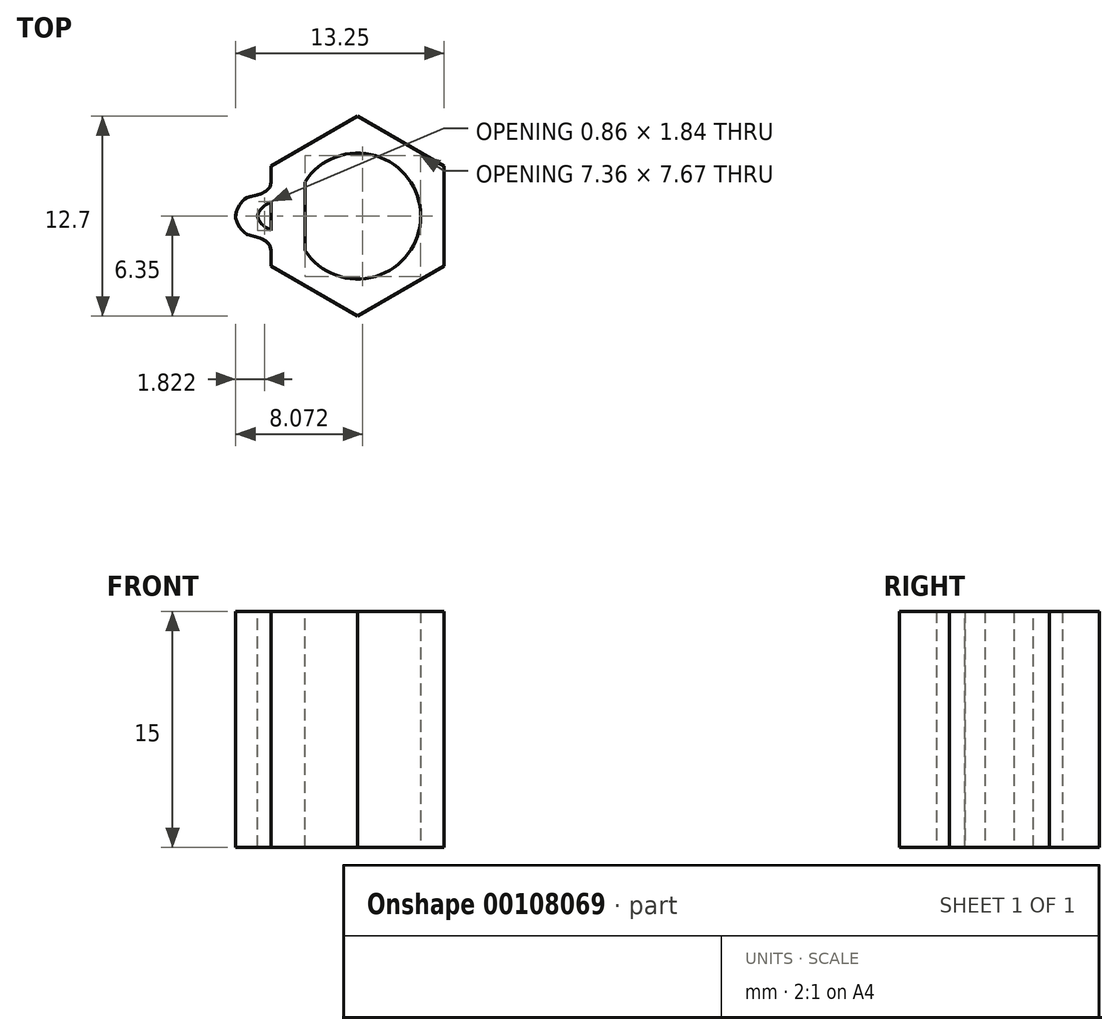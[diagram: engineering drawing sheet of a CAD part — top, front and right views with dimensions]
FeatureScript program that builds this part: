
annotation { "Feature Type Name" : "Feature", "Feature Type Description" : "" }
export const myFeature = defineFeature(function(context is Context, id is Id, definition is map)
    precondition{}
    {
        {
            var Q0;
            Q0=qCreatedBy(makeId("Top.planeOp"),FACE);
            var sketch = newSketch(context, id + "F0", { "sketchPlane" : qUnion([Q0])});
            skCircle(sketch, "E0", {"center": v(0, 0) * mm, "radius": 4 * mm});
            skCircle(sketch, "E1.cCircle", {"center": v(0, 0) * mm, "radius": 5.5 * mm, "construction": true});
            skLineSegment(sketch, "E1.0", {"start": v(5.5, 3.18) * mm, "end": v(5.5, -3.18) * mm});
            skLineSegment(sketch, "E1.1", {"start": v(5.5, -3.18) * mm, "end": v(0, -6.35) * mm});
            skLineSegment(sketch, "E1.2", {"start": v(0, -6.35) * mm, "end": v(-5.5, -3.18) * mm});
            skLineSegment(sketch, "E1.3", {"start": v(-5.5, -3.18) * mm, "end": v(-5.5, 3.18) * mm});
            skLineSegment(sketch, "E1.4", {"start": v(-5.5, 3.18) * mm, "end": v(0, 6.35) * mm});
            skLineSegment(sketch, "E1.5", {"start": v(0, 6.35) * mm, "end": v(5.5, 3.18) * mm});
            skPoint(sketch, "E1.0.midPoint", {"position": v(5.5, 0) * mm});
            skSolve(sketch);
        }
        {
            var Q0;
            Q0=makeQuery(id+"F0.imprint","IMPRINT",FACE,{"disambiguationData":[TD([[makeQuery(id+"F0.imprint","IMPRINT",EDGE,{"derivedFrom":sQuery(id+"F0.wireOp",EDGE,"E0")}),-1.0]])]});
            extrude(context, id + "F1", {"entities" : qUnion([Q0]), "depth" : 15 * mm});
        }
        {
            var Q0;
            Q0=makeQuery(id+"F1.opExtrude","CAP_FACE",FACE,{"disambiguationData":[OSD([sQuery(id+"F0.wireOp",EDGE,"E0"),sQuery(id+"F0.wireOp",EDGE,"E1.0"),sQuery(id+"F0.wireOp",EDGE,"E1.1"),sQuery(id+"F0.wireOp",EDGE,"E1.2"),sQuery(id+"F0.wireOp",EDGE,"E1.3"),sQuery(id+"F0.wireOp",EDGE,"E1.4"),sQuery(id+"F0.wireOp",EDGE,"E1.5")])],"isStart":false});
            var sketch = newSketch(context, id + "F2", { "sketchPlane" : qUnion([Q0])});
            skLineSegment(sketch, "E2", {"start": v(-5.5, 2.18) * mm, "end": v(-3.36, 2.18) * mm});
            skLineSegment(sketch, "E3", {"start": v(-5.5, -2.18) * mm, "end": v(-3.36, -2.18) * mm});
            skLineSegment(sketch, "E4", {"start": v(-5.5, 2.18) * mm, "end": v(-5.5, -2.18) * mm});
            skLineSegment(sketch, "E5", {"start": v(-3.36, 2.18) * mm, "end": v(-3.36, -2.18) * mm});
            skSolve(sketch);
        }
        {
            var Q0;
            {var subQ0=sQuery(id+"F2.wireOp",EDGE,"E2");Q0=makeQuery(id+"F2.imprint","IMPRINT",FACE,{"disambiguationData":[TD([[makeQuery(id+"F2.imprint","IMPRINT",EDGE,{"derivedFrom":subQ0}),-1.0]])]});}
            var Q1;
            Q1=makeQuery(id+"F1.opExtrude","CAP_FACE",FACE,{"disambiguationData":[OSD([sQuery(id+"F0.wireOp",EDGE,"E0"),sQuery(id+"F0.wireOp",EDGE,"E1.0"),sQuery(id+"F0.wireOp",EDGE,"E1.1"),sQuery(id+"F0.wireOp",EDGE,"E1.2"),sQuery(id+"F0.wireOp",EDGE,"E1.3"),sQuery(id+"F0.wireOp",EDGE,"E1.4"),sQuery(id+"F0.wireOp",EDGE,"E1.5")])],"isStart":true});
            extrude(context, id + "F3", {"entities" : qUnion([Q0, Q1]), "operationType" : NewBodyOperationType.REMOVE, "endBound" : BoundingType.THROUGH_ALL, "oppositeDirection" : true, "depth" : 25 * mm});
        }
        {
            var Q0;
            Q0=qCreatedBy(makeId("Top.planeOp"),FACE);
            var sketch = newSketch(context, id + "F4", { "sketchPlane" : qUnion([Q0])});
            skFitSpline(sketch, "E6", {"points": [v(-3.36, 2.18) * mm, v(-4.6, 1.25) * mm, v(-5.36, 1) * mm, v(-6.36, 0) * mm, v(-5.36, -1) * mm, v(-4.6, -1.25) * mm, v(-3.36, -2.18) * mm], "startDerivative": vector(0, -10.8) * mm, "endDerivative": vector(0, -10.8) * mm});
            skLineSegment(sketch, "E7", {"start": v(-4.6, 1.25) * mm, "end": v(-4.6, -1.25) * mm, "construction": true});
            skPoint(sketch, "E8", {"position": v(-4.6, 0) * mm});
            skLineSegment(sketch, "E9", {"start": v(-5.36, 1) * mm, "end": v(-5.36, -1) * mm, "construction": true});
            skPoint(sketch, "E10", {"position": v(-5.36, 0) * mm});
            skLineSegment(sketch, "E11", {"start": v(-3.36, 1.5) * mm, "end": v(-3.36, -1.5) * mm, "construction": true});
            skPoint(sketch, "E12", {"position": v(-3.36, 0) * mm});
            skFitSpline(sketch, "E13", {"points": [v(-5.5, 2.18) * mm, v(-6.75, 1.25) * mm, v(-7.25, 1) * mm, v(-7.75, 0) * mm, v(-7.25, -1) * mm, v(-6.75, -1.25) * mm, v(-5.5, -2.25) * mm], "startDerivative": vector(0, -9.95) * mm, "endDerivative": vector(0, -10.83) * mm});
            skLineSegment(sketch, "E14", {"start": v(-6.75, 1.25) * mm, "end": v(-6.75, -1.25) * mm, "construction": true});
            skPoint(sketch, "E15", {"position": v(-6.75, 0) * mm});
            skLineSegment(sketch, "E16", {"start": v(-7.25, 1) * mm, "end": v(-7.25, -1) * mm, "construction": true});
            skPoint(sketch, "E17", {"position": v(-7.25, 0) * mm});
            skLineSegment(sketch, "E18", {"start": v(-5.5, 1.5) * mm, "end": v(-5.5, -1.5) * mm, "construction": true});
            skPoint(sketch, "E19", {"position": v(-5.5, 0) * mm});
            skLineSegment(sketch, "E20", {"start": v(-5.5, 2.18) * mm, "end": v(-3.36, 2.18) * mm});
            skLineSegment(sketch, "E21", {"start": v(-5.5, -2.25) * mm, "end": v(-3.36, -2.18) * mm});
            skSolve(sketch);
        }
        {
            var Q0;
            Q0=makeQuery(id+"F4.imprint","IMPRINT",FACE,{"disambiguationData":[TD([[makeQuery(id+"F4.imprint","IMPRINT",EDGE,{"derivedFrom":sQuery(id+"F4.wireOp",EDGE,"E6")}),-1.0]])]});
            var Q1;
            Q1=makeQuery(id+"F1.opExtrude","CAP_FACE",FACE,{"disambiguationData":[OSD([sQuery(id+"F0.wireOp",EDGE,"E0"),sQuery(id+"F0.wireOp",EDGE,"E1.0"),sQuery(id+"F0.wireOp",EDGE,"E1.1"),sQuery(id+"F0.wireOp",EDGE,"E1.2"),sQuery(id+"F0.wireOp",EDGE,"E1.3"),sQuery(id+"F0.wireOp",EDGE,"E1.4"),sQuery(id+"F0.wireOp",EDGE,"E1.5")])],"isStart":false});
            extrude(context, id + "F5", {"entities" : qUnion([Q0]), "operationType" : NewBodyOperationType.ADD, "endBound" : BoundingType.UP_TO_SURFACE, "endBoundEntityFace" : qUnion([Q1]), "depth" : 25 * mm});
        }
        {
            var Q0;
            Q0 = qSketchRegion(id + "F2", true);
            var Q1;
            Q1=makeQuery(id+"F1.opExtrude","CAP_FACE",FACE,{"disambiguationData":[OSD([sQuery(id+"F0.wireOp",EDGE,"E0"),sQuery(id+"F0.wireOp",EDGE,"E1.0"),sQuery(id+"F0.wireOp",EDGE,"E1.1"),sQuery(id+"F0.wireOp",EDGE,"E1.2"),sQuery(id+"F0.wireOp",EDGE,"E1.3"),sQuery(id+"F0.wireOp",EDGE,"E1.4"),sQuery(id+"F0.wireOp",EDGE,"E1.5")])],"isStart":true});
            extrude(context, id + "F6", {"entities" : qUnion([Q0]), "operationType" : NewBodyOperationType.ADD, "endBound" : BoundingType.UP_TO_SURFACE, "oppositeDirection" : true, "endBoundEntityFace" : qUnion([Q1]), "depth" : 25 * mm});
        }
    });
